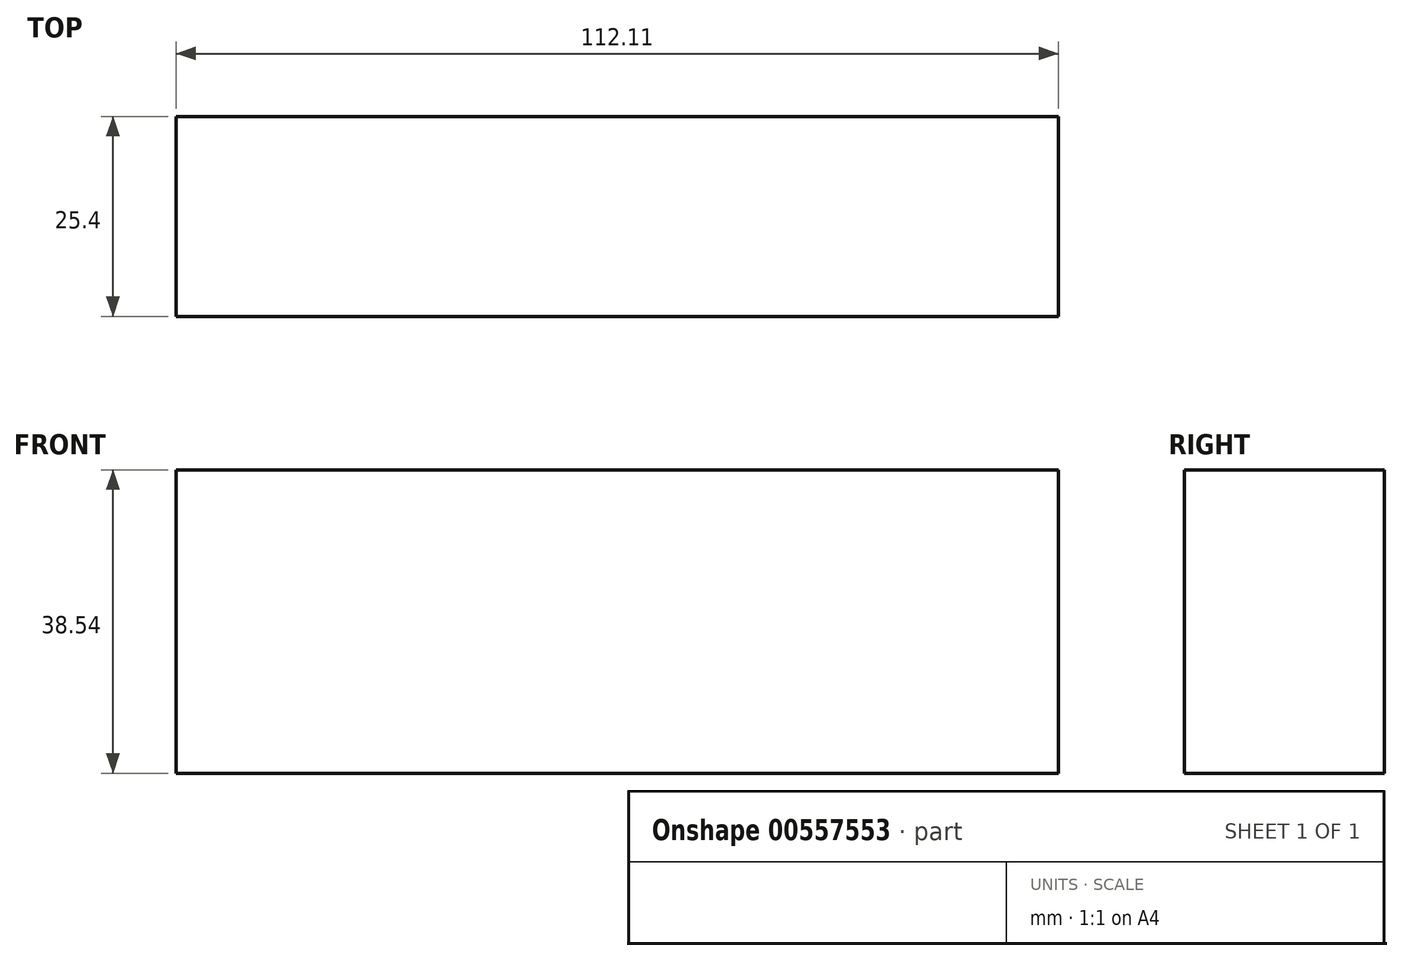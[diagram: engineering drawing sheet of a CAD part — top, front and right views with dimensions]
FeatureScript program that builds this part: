
annotation { "Feature Type Name" : "Feature", "Feature Type Description" : "" }
export const myFeature = defineFeature(function(context is Context, id is Id, definition is map)
    precondition{}
    {
        {
            var Q0;
            Q0=qCreatedBy(makeId("Front.planeOp"),FACE);
            var sketch = newSketch(context, id + "F0", { "sketchPlane" : qUnion([Q0])});
            skLineSegment(sketch, "E0.bottom", {"start": v(-7.9, 95.45) * mm, "end": v(104.2, 95.45) * mm});
            skLineSegment(sketch, "E0.top", {"start": v(-7.9, 56.91) * mm, "end": v(104.2, 56.91) * mm});
            skLineSegment(sketch, "E0.left", {"start": v(-7.9, 95.45) * mm, "end": v(-7.9, 56.91) * mm});
            skLineSegment(sketch, "E0.right", {"start": v(104.2, 95.45) * mm, "end": v(104.2, 56.91) * mm});
            skSolve(sketch);
        }
        {
            var Q0;
            Q0 = qSketchRegion(id + "F0", true);
            extrude(context, id + "F1", {"entities" : qUnion([Q0]), "depth" : 25.4 * mm, "offsetDistance" : 25.4 * mm});
        }
    });
